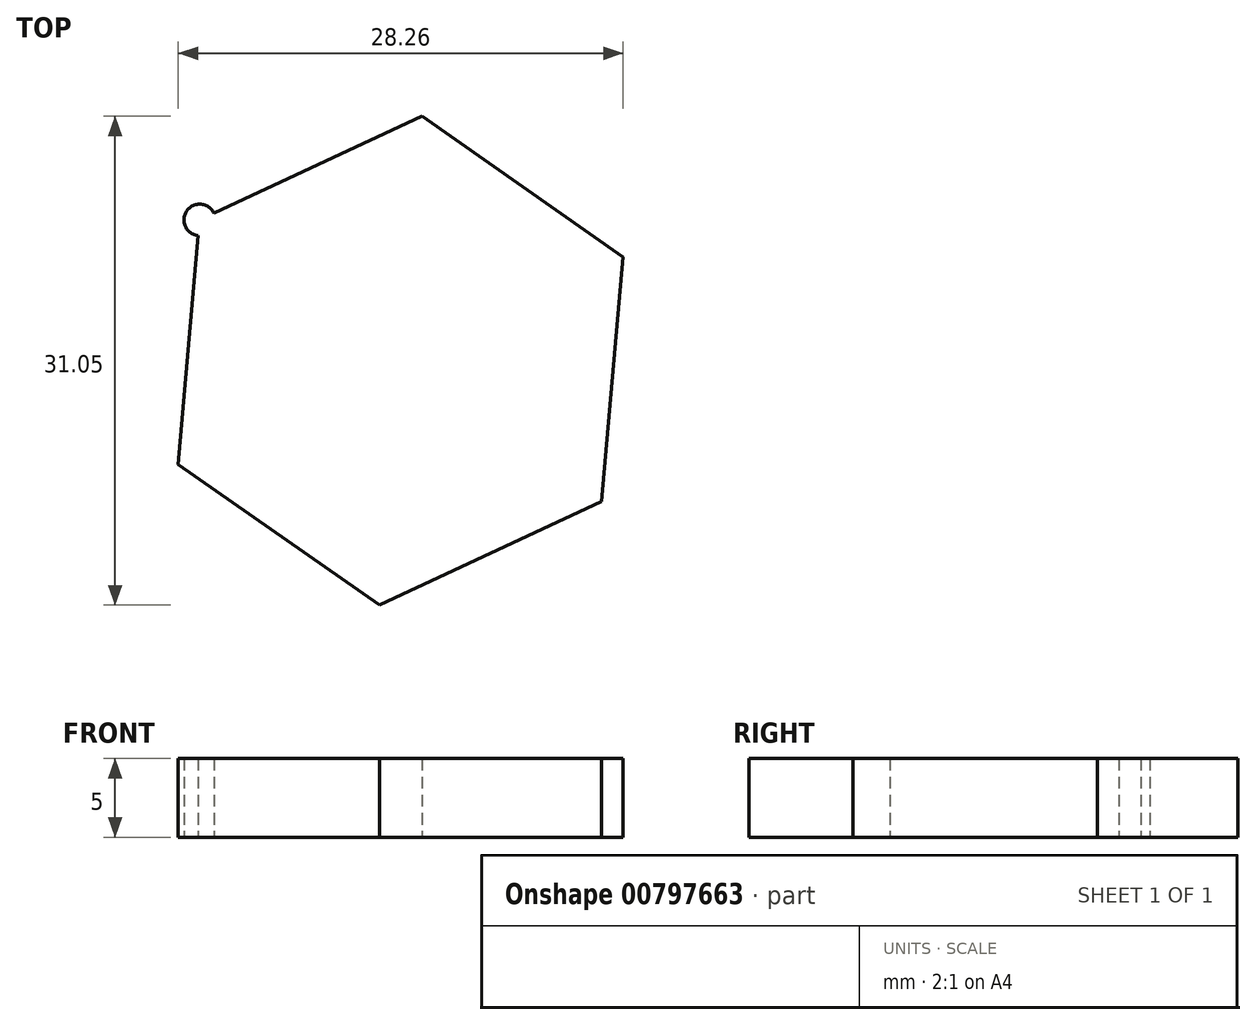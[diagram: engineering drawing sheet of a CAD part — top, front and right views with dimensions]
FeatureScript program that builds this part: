
annotation { "Feature Type Name" : "Feature", "Feature Type Description" : "" }
export const myFeature = defineFeature(function(context is Context, id is Id, definition is map)
    precondition{}
    {
        {
            var Q0;
            Q0=qCreatedBy(makeId("Top.planeOp"),FACE);
            var sketch = newSketch(context, id + "F0", { "sketchPlane" : qUnion([Q0])});
            skArc(sketch, "E0", {"start": v(-12.86, 8.65) * mm, "mid": v(-13.59, 10.22) * mm, "end": v(-11.86, 10.07) * mm});
            skLineSegment(sketch, "E1", {"start": v(-11.86, 10.07) * mm, "end": v(1.36, 16.23) * mm});
            skLineSegment(sketch, "E2", {"start": v(1.36, 16.23) * mm, "end": v(14.13, 7.3) * mm});
            skLineSegment(sketch, "E3", {"start": v(14.13, 7.3) * mm, "end": v(12.77, -8.24) * mm});
            skLineSegment(sketch, "E4", {"start": v(12.77, -8.24) * mm, "end": v(-1.36, -14.82) * mm});
            skLineSegment(sketch, "E5", {"start": v(-1.36, -14.82) * mm, "end": v(-14.13, -5.88) * mm});
            skLineSegment(sketch, "E6", {"start": v(-14.13, -5.88) * mm, "end": v(-12.86, 8.65) * mm});
            skArc(sketch, "E7", {"start": v(0, 33.7) * mm, "mid": v(-10.18, 47.2) * mm, "end": v(0, 60.7) * mm});
            skArc(sketch, "E8", {"start": v(0, 60.7) * mm, "mid": v(-5.22, 60.48) * mm, "end": v(-10.4, 59.8) * mm});
            skArc(sketch, "E9", {"start": v(-10.4, 59.8) * mm, "mid": v(-39.02, 21.28) * mm, "end": v(-22.24, -23.68) * mm});
            skArc(sketch, "E10", {"start": v(-22.24, -23.68) * mm, "mid": v(-11.92, -30.07) * mm, "end": v(0, -32.3) * mm});
            skArc(sketch, "E11", {"start": v(0, -32.3) * mm, "mid": v(10.18, -45.8) * mm, "end": v(0, -59.3) * mm});
            skArc(sketch, "E12", {"start": v(0, -59.3) * mm, "mid": v(5.22, -59.07) * mm, "end": v(10.4, -58.39) * mm});
            skArc(sketch, "E13", {"start": v(10.4, -58.39) * mm, "mid": v(39.02, -19.87) * mm, "end": v(22.24, 25.09) * mm});
            skArc(sketch, "E14", {"start": v(22.24, 25.09) * mm, "mid": v(11.92, 31.48) * mm, "end": v(0, 33.7) * mm});
            skSolve(sketch);
        }
        {
            var Q0;
            Q0=makeQuery(id+"F0.imprint","IMPRINT",FACE,{"disambiguationData":[TD([[makeQuery(id+"F0.imprint","IMPRINT",EDGE,{"derivedFrom":sQuery(id+"F0.wireOp",EDGE,"E0")}),1.0]])]});
            extrude(context, id + "F1", {"entities" : qUnion([Q0]), "depth" : 5 * mm, "offsetDistance" : 25 * mm});
        }
    });
